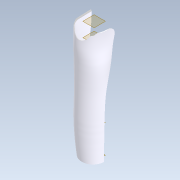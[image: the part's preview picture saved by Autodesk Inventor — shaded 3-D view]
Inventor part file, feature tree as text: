
AUTODESK INVENTOR PART (.ipt)
format: ipt  version: 2020.2 (Build 242310000, 310)  size: 495,616 bytes
history: native  units: mm
features: sketch x7, plane x6, fillet x2, loft x1, extrude x1
ambient origin geometry x8: Origin, YZ Plane, XZ Plane, XY Plane, X Axis, Y Axis, Z Axis, Center Point
bodies: Solid1 (feature_tree)
feature tree (17):
  plane  "Work Plane6"
  loft  "Loft1"
  extrude  "Extrusion1"  Depth=50.0mm
  fillet  "Fillet6"  Radius=30.0mm
  fillet  "Fillet7"  Radius=1.0mm
  plane  "Work Plane1"
  plane  "Work Plane2"
  plane  "Work Plane3"
  plane  "Work Plane4"
  plane  "Work Plane5"
  sketch  "Sketch1"  dims[d0=30.0mm d1=50.0mm]
  sketch  "Sketch2"  dims[d2=50.0mm d3=50.0mm d4=30.0mm d5=25.0mm d6=1.0mm]
  sketch  "Sketch3"  dims[d7=1.0mm]
  sketch  "Sketch4"  dims[d8=1.0mm]
  sketch  "Sketch5"  dims[d12=0.0mm d13=90.0deg]
  sketch  "Sketch6"  dims[d14=0.0mm d15=90.0deg]
  sketch  "Sketch7"  dims[d16=0.0mm d17=90.0deg d18=0.0mm d19=90.0deg d20=0.0mm d21=90.0deg d22=0.0mm d23=90.0deg d31=275.0mm d32=30.0mm d33=39.945mm d34=0.0mm d43=3.0mm d44=15.0mm d45=1.0mm d46=1.0mm d47=10.0mm d48=10.0mm]
